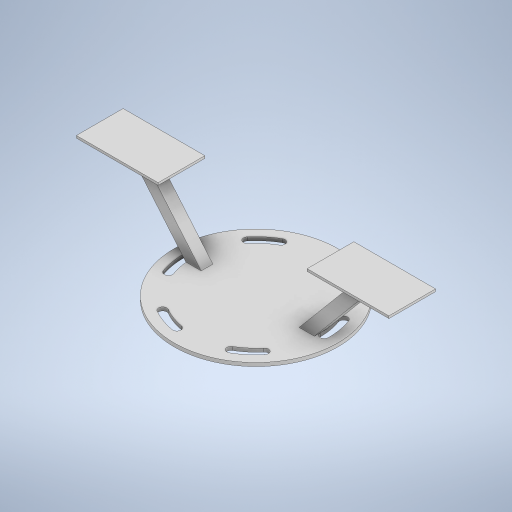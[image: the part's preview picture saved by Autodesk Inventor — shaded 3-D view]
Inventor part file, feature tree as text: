
AUTODESK INVENTOR PART (.ipt)
format: ipt  version: 2024.3 (Build 283343000, 343)  size: 309,760 bytes
history: native  units: mm
features: extrude x4, sketch x4, mirror x2, pattern_circular x1
ambient origin geometry x8: Origin, YZ Plane, XZ Plane, XY Plane, X Axis, Y Axis, Z Axis, Center Point
bodies: Solid1 (feature_tree)
feature tree (11):
  extrude  "Extrusion1"  Depth=3.0mm TaperAngle=0.0deg
  extrude  "Extrusion2"  Depth=110.0mm
  pattern_circular  "Circular Pattern1"  Count=2  [1 undecoded]
  extrude  "Extrusion3"  Depth=60.0mm TaperAngle=360.0deg
  mirror  "Mirror1"
  extrude  "Extrusion4"  Depth=60.0mm
  mirror  "Mirror2"
  sketch  "Sketch1"  dims[d0=140.0mm d1=3.0mm d2=0.0mm]
  sketch  "Sketch2"  dims[d3=124.0mm d4=110.0mm d7=20.0mm]
  sketch  "Sketch4"  dims[d8=0.0mm d9=0.0mm d10=60.0mm d11=360.0deg]
  sketch  "Sketch6"  dims[d13=8.726646mm d14=60.0mm d15=55.0mm d16=10.0mm d17=10.0mm d18=0.0mm d22=2.0mm d23=70.0mm d24=0.0mm d25=40.0mm d26=0.0mm]
note: 1 required parameter value undecoded (feature->parameter linkage not recoverable at this tier; creation-order binding heuristic only, values carry confidence <= 0.55)
